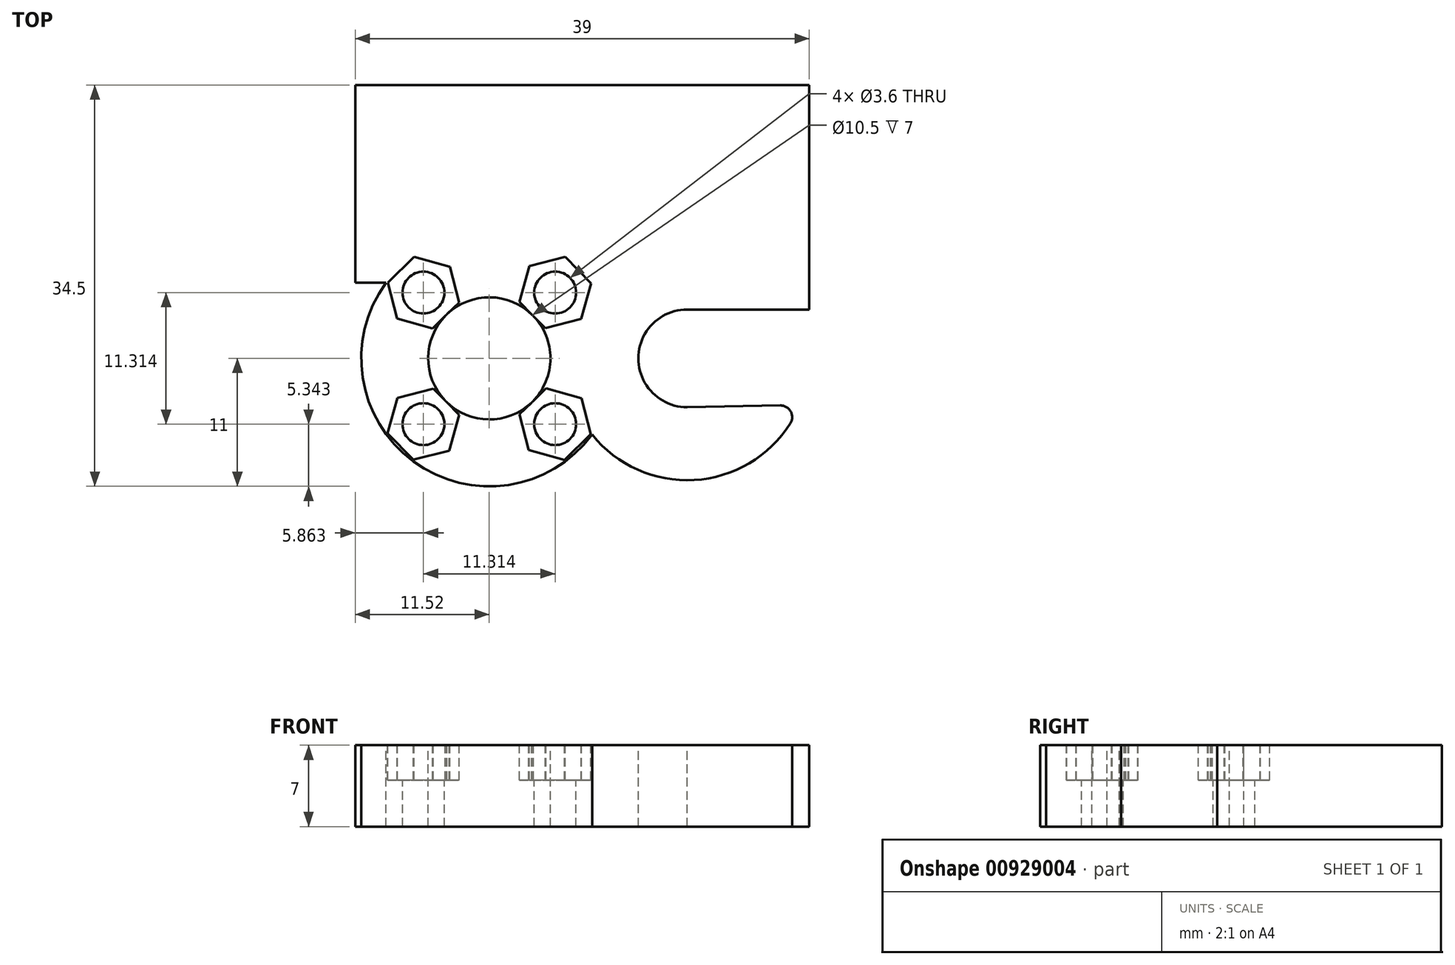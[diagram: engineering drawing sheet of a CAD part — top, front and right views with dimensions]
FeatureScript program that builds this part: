
annotation { "Feature Type Name" : "Feature", "Feature Type Description" : "" }
export const myFeature = defineFeature(function(context is Context, id is Id, definition is map)
    precondition{}
    {
        {
            var Q0;
            Q0=qCreatedBy(makeId("Top.planeOp"),FACE);
            var sketch = newSketch(context, id + "F0", { "sketchPlane" : qUnion([Q0])});
            skArc(sketch, "E0", {"start": v(17, 4.2) * mm, "mid": v(12.8, 0) * mm, "end": v(17, -4.2) * mm});
            skLineSegment(sketch, "E1.MirrorCS", {"start": v(27.48, 23.5) * mm, "end": v(-11.52, 23.5) * mm});
            skLineSegment(sketch, "E2.MirrorCS", {"start": v(-11.52, 6.5) * mm, "end": v(-8.87, 6.5) * mm});
            skCircle(sketch, "E3", {"center": v(0, 0) * mm, "radius": 5.25 * mm});
            skCircle(sketch, "E4", {"center": v(0, 0) * mm, "radius": 8 * mm, "construction": true});
            skCircle(sketch, "E5", {"center": v(-5.66, -5.66) * mm, "radius": 1.8 * mm});
            skCircle(sketch, "E6.1.0", {"center": v(5.66, -5.66) * mm, "radius": 1.8 * mm});
            skCircle(sketch, "E6.2.0", {"center": v(5.66, 5.66) * mm, "radius": 1.8 * mm});
            skCircle(sketch, "E6.3.0", {"center": v(-5.66, 5.66) * mm, "radius": 1.8 * mm});
            skLineSegment(sketch, "E7", {"start": v(25, -4.05) * mm, "end": v(17, -4.2) * mm});
            skLineSegment(sketch, "E8", {"start": v(0, -61.32) * mm, "end": v(0, 66.2) * mm, "construction": true});
            skArc(sketch, "E9.filletArc", {"start": v(25.86, -5.58) * mm, "mid": v(25.89, -4.56) * mm, "end": v(25, -4.05) * mm});
            skLineSegment(sketch, "E10", {"start": v(-25.02, 45.27) * mm, "end": v(-25.02, -15.37) * mm, "construction": true});
            skArc(sketch, "E11.MirrorCS", {"start": v(-76.51, 4.05) * mm, "mid": v(-77.22, 4.34) * mm, "end": v(-77.51, 5.05) * mm});
            skArc(sketch, "E12.MirrorCS", {"start": v(-75.9, -5.58) * mm, "mid": v(-75.93, -4.56) * mm, "end": v(-75.04, -4.05) * mm});
            skArc(sketch, "E13.MirrorCS", {"start": v(-77.51, 22.5) * mm, "mid": v(-77.22, 23.2) * mm, "end": v(-76.51, 23.5) * mm});
            skLineSegment(sketch, "E14.MirrorCS", {"start": v(-77.51, 5.05) * mm, "end": v(-77.51, 22.5) * mm});
            skPoint(sketch, "E15.MirrorP", {"position": v(-77.51, 4.05) * mm});
            skPoint(sketch, "E16.MirrorP", {"position": v(-77.51, 23.5) * mm});
            skPoint(sketch, "E17.MirrorP", {"position": v(-76.7, -4.05) * mm});
            skLineSegment(sketch, "E18", {"start": v(-11.52, 23.5) * mm, "end": v(-11.52, 6.5) * mm});
            skArc(sketch, "E19", {"start": v(-8.87, 6.5) * mm, "mid": v(-6.53, -8.85) * mm, "end": v(8.83, -6.56) * mm});
            skLineSegment(sketch, "E20", {"start": v(27.48, 23.5) * mm, "end": v(27.48, 4.2) * mm});
            skLineSegment(sketch, "E21", {"start": v(27.48, 4.2) * mm, "end": v(17, 4.2) * mm});
            skArc(sketch, "E22", {"start": v(8.83, -6.56) * mm, "mid": v(17.6, -10.46) * mm, "end": v(25.86, -5.58) * mm});
            skSolve(sketch);
        }
        {
            var Q0;
            {var subQ0=sQuery(id+"F0.wireOp",EDGE,"E0");Q0=makeQuery(id+"F0.imprint","IMPRINT",FACE,{"disambiguationData":[TD([[makeQuery(id+"F0.imprint","IMPRINT",EDGE,{"derivedFrom":subQ0}),-1.0]])]});}
            var Q1;
            Q1=makeQuery(id+"F0.imprint","IMPRINT",FACE,{"disambiguationData":[TD([[makeQuery(id+"F0.imprint","IMPRINT",EDGE,{"derivedFrom":sQuery(id+"F0.wireOp",EDGE,"56a83845-20d8-45d6-8d38-0c0d2fac5b551.MirrorCS")}),-1.0]])]});
            extrude(context, id + "F1", {"entities" : qUnion([Q0, Q1]), "oppositeDirection" : true, "depth" : 7 * mm, "offsetDistance" : 25 * mm});
        }
        {
            var Q0;
            Q0=makeQuery(id+"F1.opExtrude","CAP_FACE",FACE,{"disambiguationData":[OSD([sQuery(id+"F0.wireOp",EDGE,"E0"),sQuery(id+"F0.wireOp",EDGE,"E1.MirrorCS"),sQuery(id+"F0.wireOp",EDGE,"80a01aa0-fdad-4a96-b8b8-0ad8b2e4639c.MirrorCS"),sQuery(id+"F0.wireOp",EDGE,"E2.MirrorCS"),sQuery(id+"F0.wireOp",EDGE,"f29d9dd2-a5d6-49a9-b722-31e946dff18a"),sQuery(id+"F0.wireOp",EDGE,"E3"),sQuery(id+"F0.wireOp",EDGE,"E5"),sQuery(id+"F0.wireOp",EDGE,"E6.1.0"),sQuery(id+"F0.wireOp",EDGE,"E6.2.0"),sQuery(id+"F0.wireOp",EDGE,"E6.3.0"),sQuery(id+"F0.wireOp",EDGE,"E7"),sQuery(id+"F0.wireOp",EDGE,"967df673-8faa-42e4-90b3-42a4b1e26402"),sQuery(id+"F0.wireOp",EDGE,"0b23c685-beb4-477d-929f-ac5e8c773c9e.filletArc"),sQuery(id+"F0.wireOp",EDGE,"E9.filletArc"),sQuery(id+"F0.wireOp",EDGE,"4f09fcc4-2eee-4feb-b1c5-63993f1d4aaf.filletArc"),sQuery(id+"F0.wireOp",EDGE,"cfrKaJv5-upck-hpsf-4mJM-qhN0xd3NFZzz"),sQuery(id+"F0.wireOp",EDGE,"E18")])],"isStart":true});
            var sketch = newSketch(context, id + "F2", { "sketchPlane" : qUnion([Q0])});
            skCircle(sketch, "E23.cCircle", {"center": v(-5.66, -5.66) * mm, "radius": 2.75 * mm, "construction": true});
            skLineSegment(sketch, "E23.0", {"start": v(-8.73, -6.45) * mm, "end": v(-7.88, -3.39) * mm});
            skLineSegment(sketch, "E23.1", {"start": v(-7.88, -3.39) * mm, "end": v(-4.8, -2.6) * mm});
            skLineSegment(sketch, "E23.2", {"start": v(-4.8, -2.6) * mm, "end": v(-2.58, -4.87) * mm});
            skLineSegment(sketch, "E23.3", {"start": v(-2.58, -4.87) * mm, "end": v(-3.44, -7.93) * mm});
            skLineSegment(sketch, "E23.4", {"start": v(-3.44, -7.93) * mm, "end": v(-6.51, -8.72) * mm});
            skLineSegment(sketch, "E23.5", {"start": v(-6.51, -8.72) * mm, "end": v(-8.73, -6.45) * mm});
            skPoint(sketch, "E23.0.midPoint", {"position": v(-8.3, -4.92) * mm});
            skPoint(sketch, "E24.1.0", {"position": v(4.92, -8.3) * mm});
            skCircle(sketch, "E24.1.1", {"center": v(5.66, -5.66) * mm, "radius": 2.75 * mm, "construction": true});
            skLineSegment(sketch, "E24.1.2", {"start": v(6.45, -8.73) * mm, "end": v(3.39, -7.88) * mm});
            skLineSegment(sketch, "E24.1.3", {"start": v(4.87, -2.58) * mm, "end": v(7.93, -3.44) * mm});
            skLineSegment(sketch, "E24.1.4", {"start": v(8.72, -6.51) * mm, "end": v(6.45, -8.73) * mm});
            skLineSegment(sketch, "E24.1.5", {"start": v(2.6, -4.8) * mm, "end": v(4.87, -2.58) * mm});
            skLineSegment(sketch, "E24.1.6", {"start": v(3.39, -7.88) * mm, "end": v(2.6, -4.8) * mm});
            skLineSegment(sketch, "E24.1.7", {"start": v(7.93, -3.44) * mm, "end": v(8.72, -6.51) * mm});
            skPoint(sketch, "E24.2.0", {"position": v(8.3, 4.92) * mm});
            skCircle(sketch, "E24.2.1", {"center": v(5.66, 5.66) * mm, "radius": 2.75 * mm, "construction": true});
            skLineSegment(sketch, "E24.2.2", {"start": v(8.73, 6.45) * mm, "end": v(7.88, 3.39) * mm});
            skLineSegment(sketch, "E24.2.3", {"start": v(2.58, 4.87) * mm, "end": v(3.44, 7.93) * mm});
            skLineSegment(sketch, "E24.2.4", {"start": v(6.51, 8.72) * mm, "end": v(8.73, 6.45) * mm});
            skLineSegment(sketch, "E24.2.5", {"start": v(4.8, 2.6) * mm, "end": v(2.58, 4.87) * mm});
            skLineSegment(sketch, "E24.2.6", {"start": v(7.88, 3.39) * mm, "end": v(4.8, 2.6) * mm});
            skLineSegment(sketch, "E24.2.7", {"start": v(3.44, 7.93) * mm, "end": v(6.51, 8.72) * mm});
            skPoint(sketch, "E24.3.0", {"position": v(-4.92, 8.3) * mm});
            skCircle(sketch, "E24.3.1", {"center": v(-5.66, 5.66) * mm, "radius": 2.75 * mm, "construction": true});
            skLineSegment(sketch, "E24.3.2", {"start": v(-6.45, 8.73) * mm, "end": v(-3.39, 7.88) * mm});
            skLineSegment(sketch, "E24.3.3", {"start": v(-4.87, 2.58) * mm, "end": v(-7.93, 3.44) * mm});
            skLineSegment(sketch, "E24.3.4", {"start": v(-8.72, 6.51) * mm, "end": v(-6.45, 8.73) * mm});
            skLineSegment(sketch, "E24.3.5", {"start": v(-2.6, 4.8) * mm, "end": v(-4.87, 2.58) * mm});
            skLineSegment(sketch, "E24.3.6", {"start": v(-3.39, 7.88) * mm, "end": v(-2.6, 4.8) * mm});
            skLineSegment(sketch, "E24.3.7", {"start": v(-7.93, 3.44) * mm, "end": v(-8.72, 6.51) * mm});
            skPoint(sketch, "E24.center", {"position": v(0, 0) * mm});
            skSolve(sketch);
        }
        {
            var Q0;
            Q0=qSketchRegion(id+"F2",true);
            extrude(context, id + "F3", {"entities" : qUnion([Q0]), "operationType" : NewBodyOperationType.REMOVE, "oppositeDirection" : true, "depth" : 3 * mm, "offsetDistance" : 25 * mm});
        }
    });
